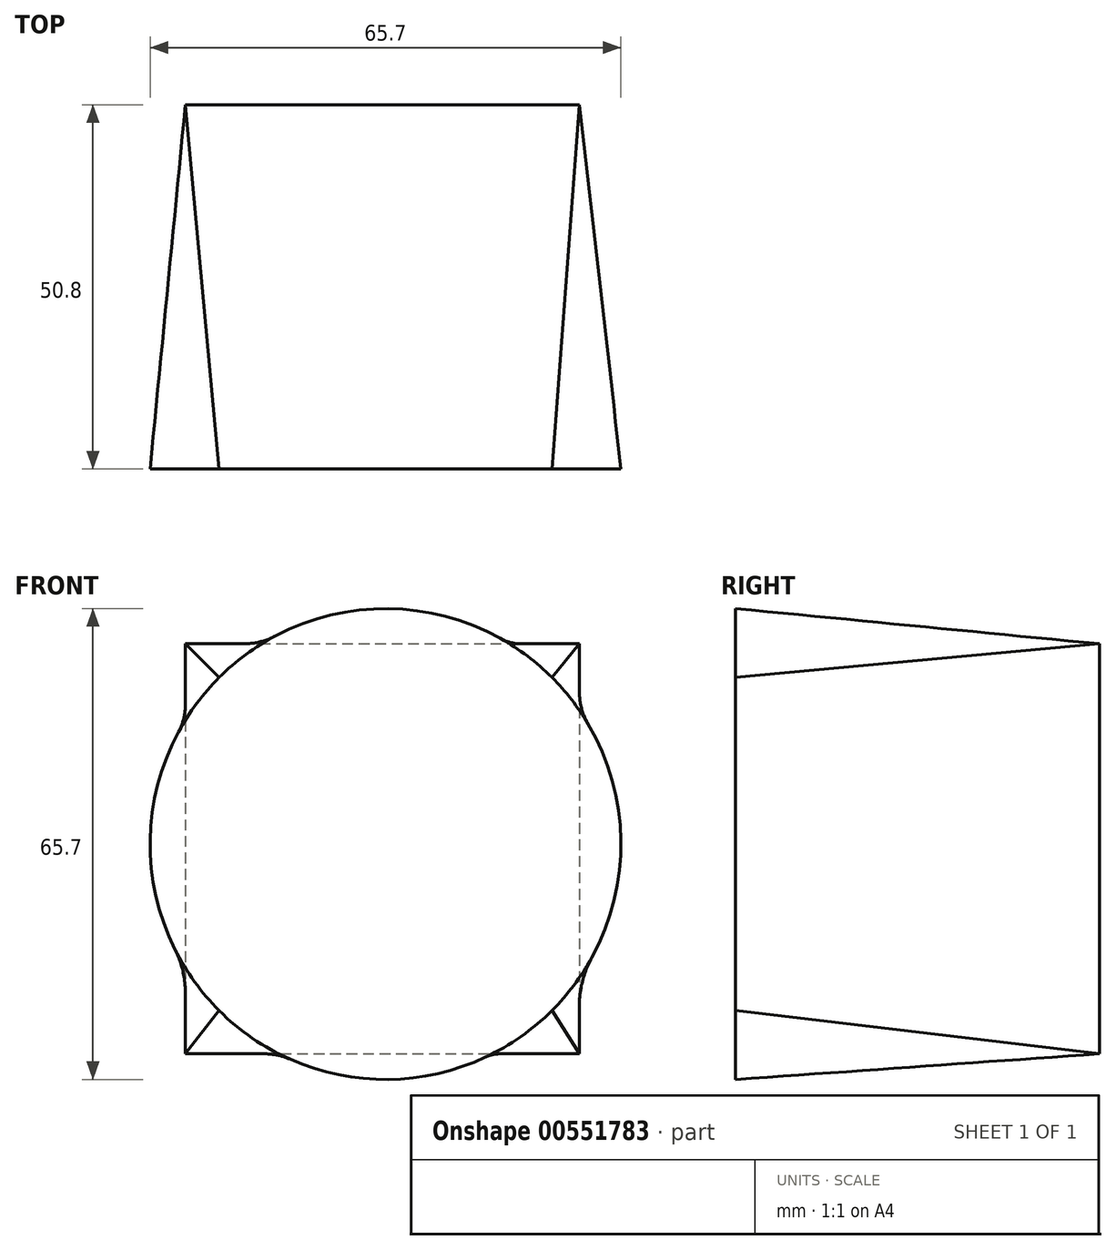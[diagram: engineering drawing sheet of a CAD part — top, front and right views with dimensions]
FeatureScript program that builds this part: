
annotation { "Feature Type Name" : "Feature", "Feature Type Description" : "" }
export const myFeature = defineFeature(function(context is Context, id is Id, definition is map)
    precondition{}
    {
        {
            var Q0;
            Q0=qCreatedBy(makeId("Front.planeOp"),FACE);
            var sketch = newSketch(context, id + "F0", { "sketchPlane" : qUnion([Q0])});
            skLineSegment(sketch, "E0.bottom", {"start": v(-27.94, 27.94) * mm, "end": v(27.04, 27.94) * mm});
            skLineSegment(sketch, "E0.top", {"start": v(-27.94, -29.28) * mm, "end": v(27.04, -29.28) * mm});
            skLineSegment(sketch, "E0.left", {"start": v(-27.94, 27.94) * mm, "end": v(-27.94, -29.28) * mm});
            skLineSegment(sketch, "E0.right", {"start": v(27.04, 27.94) * mm, "end": v(27.04, -29.28) * mm});
            skSolve(sketch);
        }
        {
            var Q0;
            Q0=qCreatedBy(makeId("Front.planeOp"),FACE);
            cPlane(context, id + "F1", {"entities" : qUnion([Q0]), "cplaneType" : CPlaneType.OFFSET, "offset" : 50.8 * mm, "width" : 152.4 * mm, "height" : 152.4 * mm});
        }
        {
            var Q0;
            Q0=qCreatedBy(id+"F1.planeOp",FACE);
            var sketch = newSketch(context, id + "F2", { "sketchPlane" : qUnion([Q0])});
            skCircle(sketch, "E1", {"center": v(0, 0) * mm, "radius": 32.85 * mm});
            skSolve(sketch);
        }
        {
            var Q0;
            Q0=makeQuery(id+"F0.imprint","IMPRINT",FACE,{"disambiguationData":[TD([[makeQuery(id+"F0.imprint","IMPRINT",EDGE,{"derivedFrom":sQuery(id+"F0.wireOp",EDGE,"E0.bottom")}),-1.0]])]});
            var Q1;
            Q1=makeQuery(id+"F2.imprint","IMPRINT",FACE,{"disambiguationData":[TD([[makeQuery(id+"F2.imprint","IMPRINT",EDGE,{"derivedFrom":sQuery(id+"F2.wireOp",EDGE,"E1")}),1.0]])]});
            loft(context, id + "F3", {"sheetProfilesArray" : [{ "sheetProfileEntities" : qUnion([Q0]) }, { "sheetProfileEntities" : qUnion([Q1]) }]});
        }
    });
